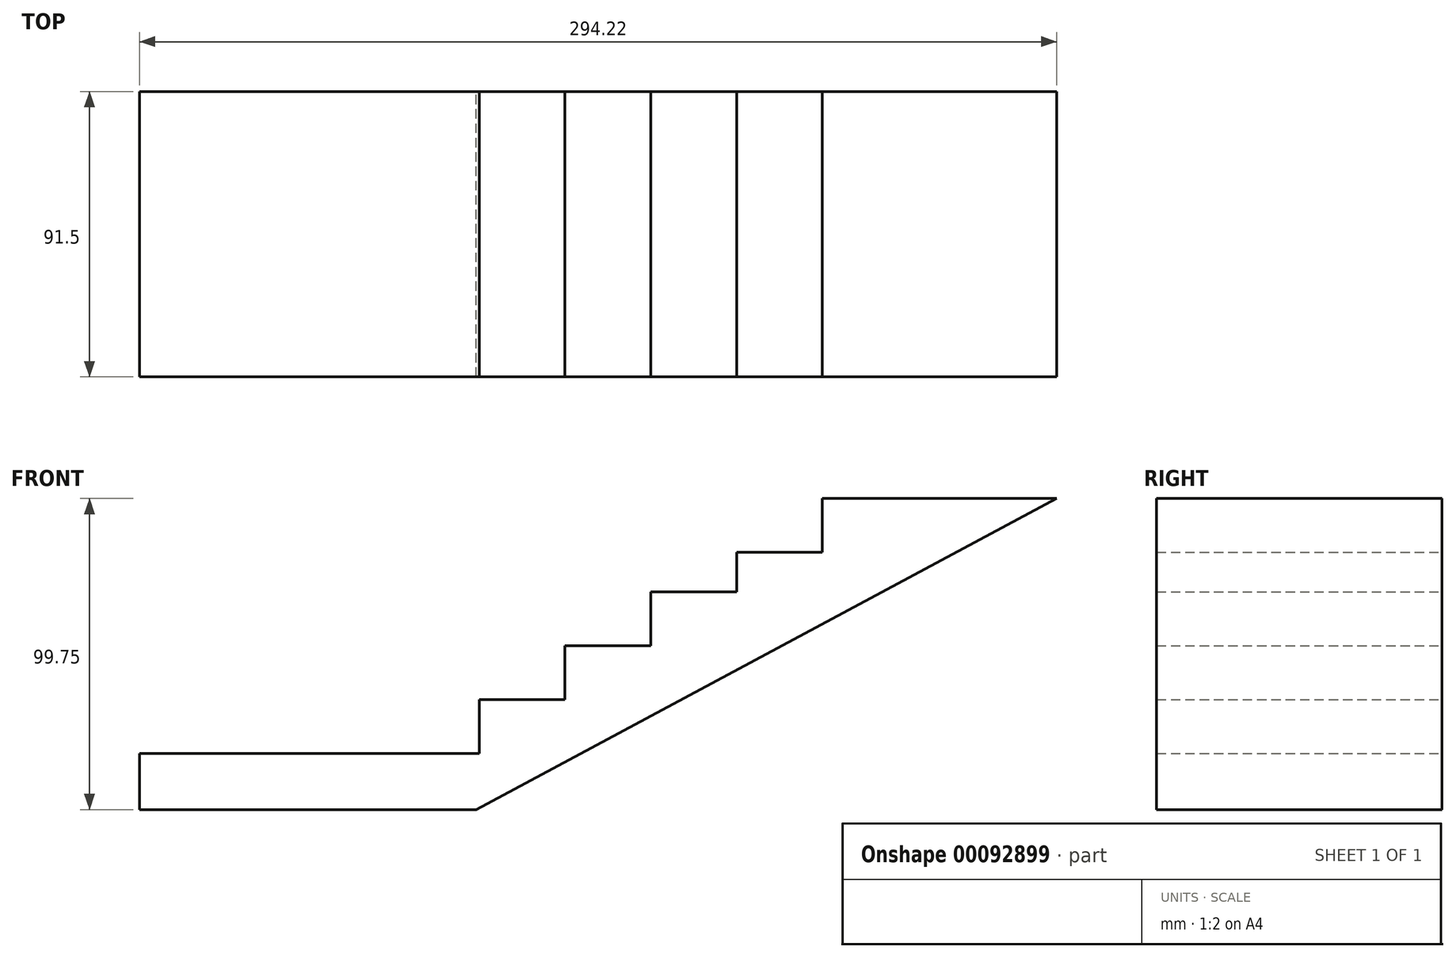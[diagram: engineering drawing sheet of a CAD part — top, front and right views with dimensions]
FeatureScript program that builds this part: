
annotation { "Feature Type Name" : "Feature", "Feature Type Description" : "" }
export const myFeature = defineFeature(function(context is Context, id is Id, definition is map)
    precondition{}
    {
        {
            var Q0;
            Q0=qCreatedBy(makeId("Front.planeOp"),FACE);
            var sketch = newSketch(context, id + "F0", { "sketchPlane" : qUnion([Q0])});
            skLineSegment(sketch, "E0", {"start": v(-55.02, -23.93) * mm, "end": v(-55.02, -6.68) * mm});
            skLineSegment(sketch, "E1", {"start": v(-55.02, -6.68) * mm, "end": v(-27.52, -6.68) * mm});
            skLineSegment(sketch, "E2", {"start": v(-27.52, -6.68) * mm, "end": v(-27.52, 10.57) * mm});
            skLineSegment(sketch, "E3", {"start": v(-27.52, 10.57) * mm, "end": v(0, 10.57) * mm});
            skLineSegment(sketch, "E4", {"start": v(0, 10.57) * mm, "end": v(0, 27.82) * mm});
            skLineSegment(sketch, "E5", {"start": v(0, 27.82) * mm, "end": v(27.5, 27.82) * mm});
            skLineSegment(sketch, "E6", {"start": v(27.5, 27.82) * mm, "end": v(27.5, 40.57) * mm});
            skLineSegment(sketch, "E7", {"start": v(27.5, 40.57) * mm, "end": v(55, 40.57) * mm});
            skLineSegment(sketch, "E8", {"start": v(55, 40.57) * mm, "end": v(55, 57.82) * mm});
            skLineSegment(sketch, "E9", {"start": v(-55.02, -23.93) * mm, "end": v(-164.02, -23.93) * mm});
            skLineSegment(sketch, "E10", {"start": v(55, 57.82) * mm, "end": v(164, 57.82) * mm});
            skLineSegment(sketch, "E11", {"start": v(-72, -23.93) * mm, "end": v(-72, -41.93) * mm});
            skLineSegment(sketch, "E12", {"start": v(-72, -41.93) * mm, "end": v(-56, -41.93) * mm});
            skLineSegment(sketch, "E13", {"start": v(-56, -41.93) * mm, "end": v(130.2, 57.82) * mm});
            skLineSegment(sketch, "E14", {"start": v(-72, -41.93) * mm, "end": v(-164.02, -41.93) * mm});
            skLineSegment(sketch, "E15", {"start": v(-164.02, -41.93) * mm, "end": v(-164.02, -23.93) * mm});
            skSolve(sketch);
        }
        {
            var Q0;
            {var subQ0=sQuery(id+"F0.wireOp",EDGE,"E0");Q0=makeQuery(id+"F0.imprint","IMPRINT",FACE,{"disambiguationData":[TD([[makeQuery(id+"F0.imprint","IMPRINT",EDGE,{"derivedFrom":subQ0}),-1.0]])]});}
            extrude(context, id + "F1", {"entities" : qUnion([Q0]), "endBound" : BoundingType.SYMMETRIC, "depth" : 91.5 * mm});
        }
        {
            var Q0;
            Q0 = qSketchRegion(id + "F0", true);
            extrude(context, id + "F2", {"entities" : qUnion([Q0]), "operationType" : NewBodyOperationType.ADD, "endBound" : BoundingType.SYMMETRIC, "depth" : 91.5 * mm});
        }
    });
